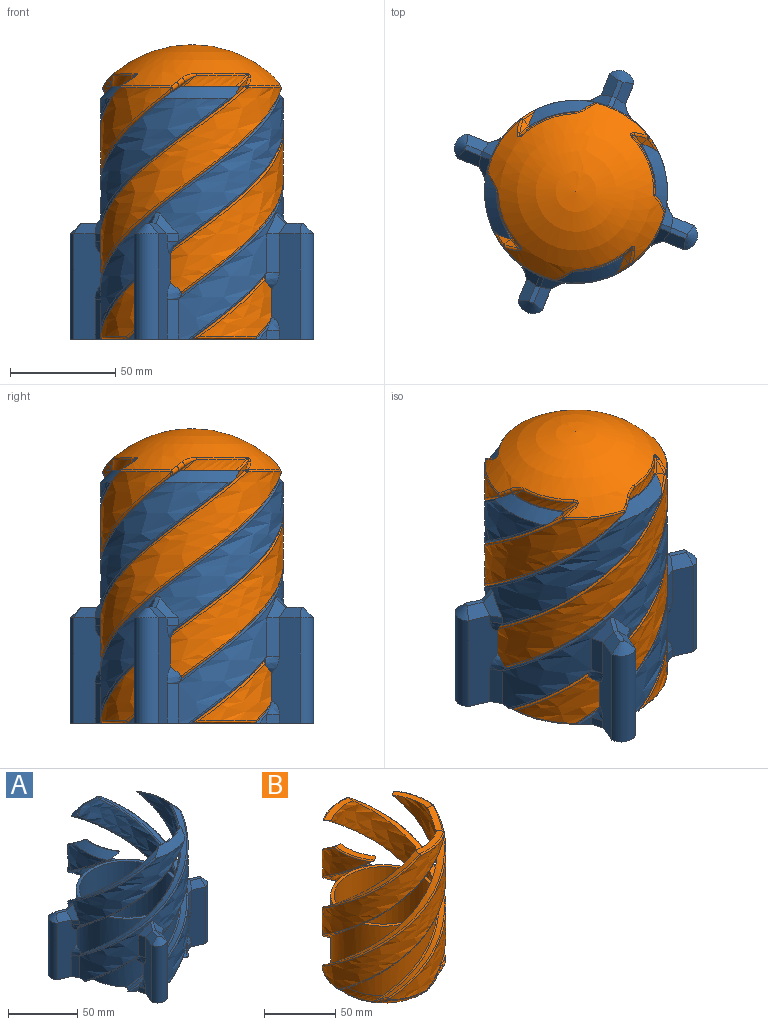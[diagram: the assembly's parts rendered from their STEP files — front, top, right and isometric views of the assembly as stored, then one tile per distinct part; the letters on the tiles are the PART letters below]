
ASSEMBLY  parts=2 mates=1
PART A: 136 faces, bbox 116.6x116.6x134.8 mm
  f0: bspline ~44.2x14.59mm, area 11.8mm2, adj f10,f52,f126
  f1: bspline ~44.2x14.59mm, area 11.8mm2, adj f10,f54,f120
  f2: bspline ~44.2x14.59mm, area 11.8mm2, adj f10,f59,f132
  f3: bspline ~120x91.09mm, area 2943.7mm2, adj f10,f42,f58,f59,f91,f93,f95,f97
  f4: bspline ~44.2x14.59mm, area 11.8mm2, adj f10,f57,f122
  f5: cylinder r=37.5mm len=70.16mm, axis (0,0,-1), area 1582.9mm2, adj f9,f10,f33,f37
  f6: cylinder r=37.5mm len=70.16mm, axis (0,0,-1), area 1582.9mm2, adj f9,f10,f36,f39
  f7: cylinder r=37.5mm len=70.16mm, axis (0,0,-1), area 1582.9mm2, adj f9,f10,f35,f38
  f8: cylinder r=37.5mm len=70.88mm, axis (0,0,-1), area 1675mm2, adj f9,f10,f21,f34
  f9: plane 75.41x75.41mm, normal (0,0,1), area 574.3mm2, adj f5,f6,f7,f8,f11,f15,f20,f21
  f10: plane 116.14x116.14mm, normal (0,0,-1), area 6103.1mm2, adj f0,f1,f2,f3,f4,f5,f6,f7
  f11: cylinder r=35mm len=70mm, axis (0,0,-1), area 11545.4mm2, adj f9,f32
  f12: plane 60x60mm, normal (0,0,1), area 2827.4mm2, adj f32
  f13: plane 28.6x7.39mm, normal (0,0,1), area 15.2mm2, adj f15,f40,f50,f51
  f14: bspline ~120x87mm, area 762.9mm2, adj f10,f34,f40,f50,f53
  f15: bspline ~80x69.6mm, area 1583mm2, adj f9,f13,f50,f51
  f16: bspline ~120x87.01mm, area 762mm2, adj f10,f33,f40,f51,f52
  f17: bspline ~120x91.09mm, area 2943.7mm2, adj f10,f40,f52,f53,f111,f113,f115,f117
  f18: plane 28.6x7.39mm, normal (0,0,1), area 15.3mm2, adj f20,f41,f48,f49
  f19: bspline ~120x87mm, area 762.9mm2, adj f10,f35,f41,f48,f55
  f20: bspline ~80x69.6mm, area 1583mm2, adj f9,f18,f48,f49
  f21: bspline ~120x87.01mm, area 854.9mm2, adj f8,f9,f10,f41,f49,f54
  f22: bspline ~120x91.09mm, area 2943.7mm2, adj f10,f41,f54,f55,f81,f83,f85,f87
  f23: plane 28.6x7.39mm, normal (0,0,1), area 15.6mm2, adj f25,f42,f46,f47
  f24: bspline ~120x87mm, area 762.9mm2, adj f10,f39,f42,f46,f58
  f25: bspline ~80x69.6mm, area 1583mm2, adj f9,f23,f46,f47
  f26: bspline ~120x87.01mm, area 762mm2, adj f10,f38,f42,f47,f59
  f27: plane 28.6x7.39mm, normal (0,0,1), area 14.2mm2, adj f30,f43,f44,f45
  f28: bspline ~120x91.09mm, area 2943.7mm2, adj f10,f43,f56,f57,f101,f103,f105,f107
  f29: bspline ~120x87mm, area 762.9mm2, adj f10,f37,f43,f44,f56
  f30: bspline ~80x69.6mm, area 1583mm2, adj f9,f27,f44,f45
  f31: bspline ~120x87.01mm, area 762mm2, adj f10,f36,f43,f45,f57
  f32: torus R=30mm, axis (0,0,1), area 1637.5mm2, adj f11,f12
  f33: bspline ~64.76x64.57mm, area 145.5mm2, adj f5,f9,f10,f16
  f34: bspline ~65.62x52.59mm, area 145.5mm2, adj f8,f9,f10,f14
  f35: bspline ~65.62x52.59mm, area 145.5mm2, adj f7,f9,f10,f19
  f36: bspline ~64.76x64.57mm, area 145.5mm2, adj f6,f9,f10,f31
  f37: bspline ~65.62x52.59mm, area 145.5mm2, adj f5,f9,f10,f29
  f38: bspline ~64.76x64.57mm, area 145.5mm2, adj f7,f9,f10,f26
  f39: bspline ~65.62x52.59mm, area 145.5mm2, adj f6,f9,f10,f24
  f40: bspline ~40.34x13.26mm, area 248.9mm2, adj f13,f14,f16,f17,f50,f51,f52,f53
  f41: bspline ~40.34x13.26mm, area 248.9mm2, adj f18,f19,f21,f22,f48,f49,f54,f55
  f42: bspline ~40.34x13.26mm, area 248.9mm2, adj f3,f23,f24,f26,f46,f47,f58,f59
  f43: bspline ~40.34x13.26mm, area 248.9mm2, adj f27,f28,f29,f31,f44,f45,f56,f57
  f44: bspline ~64.97x62.2mm, area 145.5mm2, adj f9,f27,f29,f30,f43
  f45: bspline ~64.11x56.76mm, area 145.1mm2, adj f9,f27,f30,f31,f43
  f46: bspline ~64.97x62.2mm, area 145.5mm2, adj f9,f23,f24,f25,f42
  f47: bspline ~64.11x56.76mm, area 145.1mm2, adj f9,f23,f25,f26,f42
  f48: bspline ~64.97x62.2mm, area 145.5mm2, adj f9,f18,f19,f20,f41
  f49: bspline ~64.11x56.76mm, area 145.1mm2, adj f9,f18,f20,f21,f41
  f50: bspline ~64.97x62.2mm, area 145.5mm2, adj f9,f13,f14,f15,f40
  f51: bspline ~64.11x56.76mm, area 145.1mm2, adj f9,f13,f15,f16,f40
  f52: bspline ~117.61x85.66mm, area 305.6mm2, adj f0,f10,f16,f17,f40,f75
  f53: bspline ~118.45x87.02mm, area 306mm2, adj f10,f14,f17,f40,f70
  f54: bspline ~117.61x85.66mm, area 305.6mm2, adj f1,f10,f21,f22,f41,f70
  f55: bspline ~118.45x87.02mm, area 306mm2, adj f10,f19,f22,f41,f65
  f56: bspline ~118.45x87.02mm, area 306mm2, adj f10,f28,f29,f43,f75
  f57: bspline ~117.61x85.66mm, area 305.6mm2, adj f4,f10,f28,f31,f43,f61
  f58: bspline ~118.45x87.02mm, area 306mm2, adj f3,f10,f24,f42,f61
  f59: bspline ~117.61x85.66mm, area 305.6mm2, adj f2,f3,f10,f26,f42,f65
  f60: plane 50.04x13.84mm, normal (-0.38,-0.92,0), area 610.2mm2, adj f10,f61,f63,f96,f98,f99,f122,f123
  f61: cylinder r=43.5mm len=42.3mm, axis (0,0,-1), area 424.3mm2, adj f57,f58,f60,f62,f90,f98,f123,f125
  f62: plane 50.04x13.97mm, normal (0.38,0.92,0), area 620.4mm2, adj f10,f61,f63,f90,f91,f92,f124,f125
  f63: cylinder r=6.94mm len=50mm, axis (0,0,-1), area 760.7mm2, adj f10,f60,f62,f94
  f64: plane 8.3x5.22mm, normal (0,0,1), area 19.3mm2, adj f92,f94,f95,f96
  f65: cylinder r=43.5mm len=42.3mm, axis (0,0,-1), area 424.3mm2, adj f55,f59,f66,f68,f80,f88,f131,f133
  f66: plane 50.04x13.97mm, normal (0.92,-0.38,0), area 620.4mm2, adj f10,f65,f67,f80,f81,f82,f130,f131
  f67: cylinder r=6.94mm len=50mm, axis (0,0,-1), area 760.7mm2, adj f10,f66,f68,f84
  f68: plane 50.04x13.84mm, normal (-0.92,0.38,0), area 610.2mm2, adj f10,f65,f67,f86,f88,f89,f132,f133
  f69: plane 8.3x5.22mm, normal (0,0,1), area 19.3mm2, adj f82,f84,f85,f86
  f70: cylinder r=43.5mm len=42.3mm, axis (0,0,-1), area 424.3mm2, adj f53,f54,f71,f73,f110,f118,f121,f135
  f71: plane 50.04x13.97mm, normal (-0.38,-0.92,0), area 620.4mm2, adj f10,f70,f72,f110,f111,f112,f134,f135
  f72: cylinder r=6.94mm len=50mm, axis (0,0,-1), area 760.7mm2, adj f10,f71,f73,f114
  f73: plane 50.04x13.84mm, normal (0.38,0.92,0), area 610.2mm2, adj f10,f70,f72,f116,f118,f119,f120,f121
  f74: plane 8.3x5.22mm, normal (0,0,1), area 19.3mm2, adj f112,f114,f115,f116
  f75: cylinder r=43.5mm len=42.3mm, axis (0,0,-1), area 424.3mm2, adj f52,f56,f76,f78,f100,f108,f127,f129
  f76: plane 50.04x13.97mm, normal (-0.92,0.38,0), area 620.4mm2, adj f10,f75,f77,f100,f101,f102,f128,f129
  f77: cylinder r=6.94mm len=50mm, axis (0,0,-1), area 760.7mm2, adj f10,f76,f78,f104
  f78: plane 50.04x13.84mm, normal (0.92,-0.38,0), area 610.2mm2, adj f10,f75,f77,f106,f108,f109,f126,f127
  f79: plane 8.3x5.22mm, normal (0,0,1), area 19.3mm2, adj f102,f104,f105,f106
  f80: bspline ~6.52x6.1mm, area 17.3mm2, adj f65,f66,f81
  f81: bspline ~7.77x5.37mm, area 21.7mm2, adj f22,f66,f80,f83
  f82: plane 11.66x9.09mm, normal (0.65,-0.27,0.71), area 67.7mm2, adj f66,f69,f83,f84
  f83: bspline ~10.59x10.05mm, area 60.1mm2, adj f22,f81,f82,f85
  f84: cone r=6.94mm half-angle=45deg, axis (0,0,-1), area 57.4mm2, adj f67,f69,f82,f86
  f85: bspline ~5.47x5mm, area 15.8mm2, adj f22,f69,f83,f87
  f86: plane 11.26x9.17mm, normal (-0.65,0.27,0.71), area 66.8mm2, adj f68,f69,f84,f87
  f87: bspline ~10x9.01mm, area 60.4mm2, adj f22,f85,f86,f89
  f88: bspline ~8.78x7.69mm, area 26.9mm2, adj f65,f68,f89
  f89: bspline ~20.71x6mm, area 114.5mm2, adj f22,f68,f87,f88
  f90: bspline ~6.52x6.1mm, area 17.3mm2, adj f61,f62,f91
  f91: bspline ~7.77x5.37mm, area 21.7mm2, adj f3,f62,f90,f93
  f92: plane 11.66x9.09mm, normal (0.27,0.65,0.71), area 67.7mm2, adj f62,f64,f93,f94
  f93: bspline ~10.59x10.05mm, area 60.1mm2, adj f3,f91,f92,f95
  f94: cone r=6.94mm half-angle=45deg, axis (0,0,-1), area 57.4mm2, adj f63,f64,f92,f96
  f95: bspline ~5.47x5mm, area 15.8mm2, adj f3,f64,f93,f97
  f96: plane 11.26x9.17mm, normal (-0.27,-0.65,0.71), area 66.8mm2, adj f60,f64,f94,f97
  f97: bspline ~10x9.01mm, area 60.4mm2, adj f3,f95,f96,f99
  f98: bspline ~8.78x7.69mm, area 26.9mm2, adj f60,f61,f99
  f99: bspline ~20.71x6mm, area 114.5mm2, adj f3,f60,f97,f98
  f100: bspline ~6.52x6.1mm, area 17.3mm2, adj f75,f76,f101
  f101: bspline ~7.77x5.37mm, area 21.7mm2, adj f28,f76,f100,f103
  f102: plane 11.66x9.09mm, normal (-0.65,0.27,0.71), area 67.7mm2, adj f76,f79,f103,f104
  f103: bspline ~10.59x10.05mm, area 60.1mm2, adj f28,f101,f102,f105
  f104: cone r=6.94mm half-angle=45deg, axis (0,0,-1), area 57.4mm2, adj f77,f79,f102,f106
  f105: bspline ~5.47x5mm, area 15.8mm2, adj f28,f79,f103,f107
  f106: plane 11.26x9.17mm, normal (0.65,-0.27,0.71), area 66.8mm2, adj f78,f79,f104,f107
  f107: bspline ~10x9.01mm, area 60.4mm2, adj f28,f105,f106,f109
  f108: bspline ~8.78x7.69mm, area 26.9mm2, adj f75,f78,f109
  f109: bspline ~20.71x6mm, area 114.5mm2, adj f28,f78,f107,f108
  f110: bspline ~6.52x6.1mm, area 17.3mm2, adj f70,f71,f111
  f111: bspline ~7.77x5.37mm, area 21.7mm2, adj f17,f71,f110,f113
  f112: plane 11.66x9.09mm, normal (-0.27,-0.65,0.71), area 67.7mm2, adj f71,f74,f113,f114
  f113: bspline ~10.59x10.05mm, area 60.1mm2, adj f17,f111,f112,f115
  f114: cone r=6.94mm half-angle=45deg, axis (0,0,-1), area 57.4mm2, adj f72,f74,f112,f116
  f115: bspline ~5.47x5mm, area 15.8mm2, adj f17,f74,f113,f117
  f116: plane 11.26x9.17mm, normal (0.27,0.65,0.71), area 66.8mm2, adj f73,f74,f114,f117
  f117: bspline ~10x9.01mm, area 60.4mm2, adj f17,f115,f116,f119
  f118: bspline ~8.78x7.69mm, area 26.9mm2, adj f70,f73,f119
  f119: bspline ~20.71x6mm, area 114.5mm2, adj f17,f73,f117,f118
  f120: bspline ~6.06x4.81mm, area 26mm2, adj f1,f10,f73,f121
  f121: bspline ~6.61x6.07mm, area 17.9mm2, adj f70,f73,f120
  f122: bspline ~6.06x4.81mm, area 26mm2, adj f4,f10,f60,f123
  f123: bspline ~6.61x6.07mm, area 17.9mm2, adj f60,f61,f122
  f124: bspline ~20.21x5.43mm, area 116.9mm2, adj f10,f28,f62,f125
  f125: bspline ~9.11x7.69mm, area 26.4mm2, adj f61,f62,f124
  f126: bspline ~6.06x4.81mm, area 26mm2, adj f0,f10,f78,f127
  f127: bspline ~6.61x6.07mm, area 17.9mm2, adj f75,f78,f126
  f128: bspline ~20.21x5.43mm, area 116.9mm2, adj f10,f17,f76,f129
  f129: bspline ~9.11x7.69mm, area 26.4mm2, adj f75,f76,f128
  f130: bspline ~20.21x5.43mm, area 116.9mm2, adj f3,f10,f66,f131
  f131: bspline ~9.11x7.69mm, area 26.4mm2, adj f65,f66,f130
  f132: bspline ~6.06x4.81mm, area 26mm2, adj f2,f10,f68,f133
  f133: bspline ~6.61x6.07mm, area 17.9mm2, adj f65,f68,f132
  f134: bspline ~20.21x5.43mm, area 116.9mm2, adj f10,f22,f71,f135
  f135: bspline ~9.11x7.69mm, area 26.4mm2, adj f70,f71,f134
PART B: 114 faces, bbox 91.5x91.5x150.4 mm
  f0: cylinder r=37.5mm len=70.16mm, axis (0,0,-1), area 1582.9mm2, adj f4,f28,f32,f52
  f1: cylinder r=37.5mm len=70.16mm, axis (0,0,-1), area 1582.9mm2, adj f4,f31,f34,f47
  f2: cylinder r=37.5mm len=70.16mm, axis (0,0,-1), area 1582.9mm2, adj f4,f30,f33,f38
  f3: cylinder r=37.5mm len=70.88mm, axis (0,0,-1), area 1675mm2, adj f4,f15,f29,f43
  f4: plane 75.41x75.41mm, normal (0,0,1), area 571.7mm2, adj f0,f1,f2,f3,f5,f8,f9,f10
  f5: cylinder r=35mm len=70mm, axis (0,0,-1), area 11545.4mm2, adj f4,f27
  f6: plane 60x60mm, normal (0,0,1), area 2827.4mm2, adj f27
  f7: plane 31.81x12.32mm, normal (0,0,1), area 157.1mm2, adj f8,f9,f10,f101,f102,f103
  f8: bspline ~130x87mm, area 869.9mm2, adj f4,f7,f9,f29,f41,f101
  f9: bspline ~80x69.6mm, area 1767.1mm2, adj f4,f7,f8,f10
  f10: bspline ~130x88.08mm, area 865.8mm2, adj f4,f7,f9,f28,f54,f71,f103
  f11: bspline ~120x91.09mm, area 3641.4mm2, adj f69,f99,f100,f101,f102,f103,f104
  f12: plane 31.81x12.32mm, normal (0,0,1), area 157.1mm2, adj f13,f14,f15,f85,f86,f87
  f13: bspline ~130x87mm, area 869.9mm2, adj f4,f12,f14,f30,f36,f85
  f14: bspline ~80x69.6mm, area 1767.1mm2, adj f4,f12,f13,f15
  f15: bspline ~130x88.08mm, area 958.8mm2, adj f3,f12,f14,f44,f59,f87
  f16: bspline ~120x91.09mm, area 3641.4mm2, adj f57,f83,f84,f85,f86,f87,f88
  f17: plane 31.81x12.32mm, normal (0,0,1), area 157.1mm2, adj f19,f20,f21,f92,f93,f94
  f18: bspline ~120x91.09mm, area 3641.4mm2, adj f66,f91,f92,f93,f94,f95,f96
  f19: bspline ~130x87mm, area 869.9mm2, adj f4,f17,f20,f34,f45,f94
  f20: bspline ~80x69.6mm, area 1767.1mm2, adj f4,f17,f19,f21
  f21: bspline ~130x88.08mm, area 865.8mm2, adj f4,f17,f20,f33,f40,f64,f92
  f22: plane 31.81x12.32mm, normal (0,0,1), area 157.1mm2, adj f24,f25,f26,f108,f109,f110
  f23: bspline ~120x91.09mm, area 3641.4mm2, adj f80,f107,f108,f109,f110,f111,f112
  f24: bspline ~130x87mm, area 869.9mm2, adj f4,f22,f25,f32,f50,f110
  f25: bspline ~80x69.6mm, area 1767.1mm2, adj f4,f22,f24,f26
  f26: bspline ~130x88.08mm, area 865.8mm2, adj f4,f22,f25,f31,f49,f78,f108
  f27: torus R=30mm, axis (0,0,1), area 1637.5mm2, adj f5,f6
  f28: bspline ~64.76x64.57mm, area 145.5mm2, adj f0,f4,f10,f53
  f29: bspline ~65.62x52.59mm, area 145.5mm2, adj f3,f4,f8,f42
  f30: bspline ~65.62x52.59mm, area 145.5mm2, adj f2,f4,f13,f37
  f31: bspline ~64.76x64.57mm, area 145.5mm2, adj f1,f4,f26,f48
  f32: bspline ~65.62x52.59mm, area 145.5mm2, adj f0,f4,f24,f51
  f33: bspline ~64.76x64.57mm, area 145.5mm2, adj f2,f4,f21,f39
  f34: bspline ~65.62x52.59mm, area 145.5mm2, adj f1,f4,f19,f46
  f35: sphere r=57.31mm, area 5821.8mm2, adj f55,f56,f57,f58,f59,f60,f61,f62
  f36: bspline ~13.44x10mm, area 14.3mm2, adj f13,f37,f55,f84
  f37: bspline ~8.3x5.63mm, area 12.8mm2, adj f30,f36,f38,f56
  f38: bspline ~35.53x11.19mm, area 140.8mm2, adj f2,f37,f39,f58
  f39: bspline ~18.91x16.67mm, area 8.5mm2, adj f33,f38,f40,f60
  f40: bspline ~13.28x11.54mm, area 2.9mm2, adj f21,f39,f62
  f41: bspline ~5.65x4.34mm, area 14.3mm2, adj f8,f42,f67,f100
  f42: bspline ~20.92x16.67mm, area 12.8mm2, adj f29,f41,f43,f65
  f43: bspline ~37.92x13.6mm, area 151mm2, adj f3,f42,f44,f61,f63
  f44: bspline ~13.73x12.24mm, area 6.5mm2, adj f15,f43,f61
  f45: bspline ~5.65x4.34mm, area 14.3mm2, adj f19,f46,f68,f95
  f46: bspline ~20.92x16.67mm, area 12.8mm2, adj f34,f45,f47,f70
  f47: bspline ~35.53x11.19mm, area 140.8mm2, adj f1,f46,f48,f72
  f48: bspline ~6.77x5.34mm, area 8.5mm2, adj f31,f47,f49,f74
  f49: bspline ~13.28x11.54mm, area 2.9mm2, adj f26,f48,f76
  f50: bspline ~13.44x10mm, area 14.3mm2, adj f24,f51,f81,f111
  f51: bspline ~20.92x16.67mm, area 12.8mm2, adj f32,f50,f52,f79
  f52: bspline ~35.53x11.19mm, area 140.8mm2, adj f0,f51,f53,f77
  f53: bspline ~18.91x16.67mm, area 8.5mm2, adj f28,f52,f54,f75
  f54: bspline ~13.28x11.54mm, area 2.9mm2, adj f10,f53,f73
  f55: bspline ~9.43x8.02mm, area 11.4mm2, adj f35,f36,f56,f82,f83
  f56: bspline ~2.5x2.37mm, area 4.3mm2, adj f35,f37,f55,f58
  f57: bspline ~29.45x11.78mm, area 31.7mm2, adj f16,f35,f82,f89
  f58: bspline ~25.19x6.51mm, area 34.3mm2, adj f35,f38,f56,f60
  f59: bspline ~8.95x7.09mm, area 12.2mm2, adj f15,f35,f61,f88,f89
  f60: bspline ~6.83x4.57mm, area 15.8mm2, adj f35,f39,f58,f62
  f61: bspline ~11.03x8.3mm, area 22.9mm2, adj f35,f43,f44,f59,f63
  f62: bspline ~6.98x5.76mm, area 12mm2, adj f35,f40,f60,f64
  f63: bspline ~29.61x9.48mm, area 39.1mm2, adj f35,f43,f61,f65
  f64: bspline ~8.95x7.09mm, area 12.2mm2, adj f21,f35,f62,f90,f91
  f65: bspline ~2.5x2.37mm, area 4.3mm2, adj f35,f42,f63,f67
  f66: bspline ~29.45x11.78mm, area 31.7mm2, adj f18,f35,f90,f97
  f67: bspline ~9.43x8.02mm, area 11.4mm2, adj f35,f41,f65,f98,f99
  f68: bspline ~9.43x8.02mm, area 11.4mm2, adj f35,f45,f70,f96,f97
  f69: bspline ~29.45x11.78mm, area 31.7mm2, adj f11,f35,f98,f105
  f70: bspline ~2.5x2.37mm, area 4.3mm2, adj f35,f46,f68,f72
  f71: bspline ~8.95x7.09mm, area 12.2mm2, adj f10,f35,f73,f104,f105
  f72: bspline ~25.19x6.51mm, area 34.3mm2, adj f35,f47,f70,f74
  f73: bspline ~6.98x5.76mm, area 12mm2, adj f35,f54,f71,f75
  f74: bspline ~6.83x4.57mm, area 15.8mm2, adj f35,f48,f72,f76
  f75: bspline ~6.9x4.61mm, area 15.8mm2, adj f35,f53,f73,f77
  f76: bspline ~6.98x5.76mm, area 12mm2, adj f35,f49,f74,f78
  f77: bspline ~25.5x6.62mm, area 34.3mm2, adj f35,f52,f75,f79
  f78: bspline ~7.61x6.23mm, area 12.2mm2, adj f26,f35,f76,f106,f107
  f79: bspline ~2.5x2.37mm, area 4.3mm2, adj f35,f51,f77,f81
  f80: bspline ~29.45x11.78mm, area 31.7mm2, adj f23,f35,f106,f113
  f81: bspline ~9.43x8.02mm, area 11.4mm2, adj f35,f50,f79,f112,f113
  f82: bspline ~1.57x1.3mm, area 0.8mm2, adj f55,f57,f83
  f83: bspline ~1.34x1.2mm, area 0.6mm2, adj f16,f55,f82,f84
  f84: bspline ~6.93x5.43mm, area 0.2mm2, adj f16,f36,f83,f85
  f85: bspline ~121.66x87.02mm, area 317.4mm2, adj f12,f13,f16,f84,f86
  f86: bspline ~33.55x9.59mm, area 50.5mm2, adj f12,f16,f85,f87
  f87: bspline ~120.26x86.79mm, area 312.7mm2, adj f12,f15,f16,f86,f88
  f88: bspline ~2.22x1.26mm, area 1.7mm2, adj f16,f59,f87,f89
  f89: bspline ~1.33x0.68mm, area 0.2mm2, adj f57,f59,f88
  f90: bspline ~1.33x0.68mm, area 0.2mm2, adj f64,f66,f91
  f91: bspline ~2.22x1.26mm, area 1.7mm2, adj f18,f64,f90,f92
  f92: bspline ~120.26x86.79mm, area 312.7mm2, adj f17,f18,f21,f91,f93
  f93: bspline ~33.55x9.59mm, area 50.5mm2, adj f17,f18,f92,f94
  f94: bspline ~121.66x87.02mm, area 317.4mm2, adj f17,f18,f19,f93,f95
  f95: bspline ~6.93x5.43mm, area 0.2mm2, adj f18,f45,f94,f96
  f96: bspline ~1.34x1.2mm, area 0.6mm2, adj f18,f68,f95,f97
  f97: bspline ~1.57x1.3mm, area 0.8mm2, adj f66,f68,f96
  f98: bspline ~1.57x1.3mm, area 0.8mm2, adj f67,f69,f99
  f99: bspline ~1.34x1.2mm, area 0.6mm2, adj f11,f67,f98,f100
  f100: bspline ~6.93x5.43mm, area 0.2mm2, adj f11,f41,f99,f101
  f101: bspline ~121.66x87.02mm, area 317.4mm2, adj f7,f8,f11,f100,f102
  f102: bspline ~33.55x9.59mm, area 50.5mm2, adj f7,f11,f101,f103
  f103: bspline ~120.26x86.79mm, area 312.7mm2, adj f7,f10,f11,f102,f104
  f104: bspline ~2.22x1.26mm, area 1.7mm2, adj f11,f71,f103,f105
  f105: bspline ~1.33x0.68mm, area 0.2mm2, adj f69,f71,f104
  f106: bspline ~1.33x0.68mm, area 0.2mm2, adj f78,f80,f107
  f107: bspline ~2.22x1.26mm, area 1.7mm2, adj f23,f78,f106,f108
  f108: bspline ~120.26x86.79mm, area 312.7mm2, adj f22,f23,f26,f107,f109
  f109: bspline ~33.55x9.59mm, area 50.5mm2, adj f22,f23,f108,f110
  f110: bspline ~121.66x87.02mm, area 317.4mm2, adj f22,f23,f24,f109,f111
  f111: bspline ~6.93x5.43mm, area 0.2mm2, adj f23,f50,f110,f112
  f112: bspline ~1.34x1.2mm, area 0.6mm2, adj f23,f81,f111,f113
  f113: bspline ~1.57x1.3mm, area 0.8mm2, adj f80,f81,f112
PLACE A at identity fixed
PLACE B rot(axis=(-0.45,-0.89,0),180deg) t=(80.83,58.88,120)mm
MATE cylindrical B.f0 <-> A.f5  axis (0,0,-1) through (0,0,60)mm
